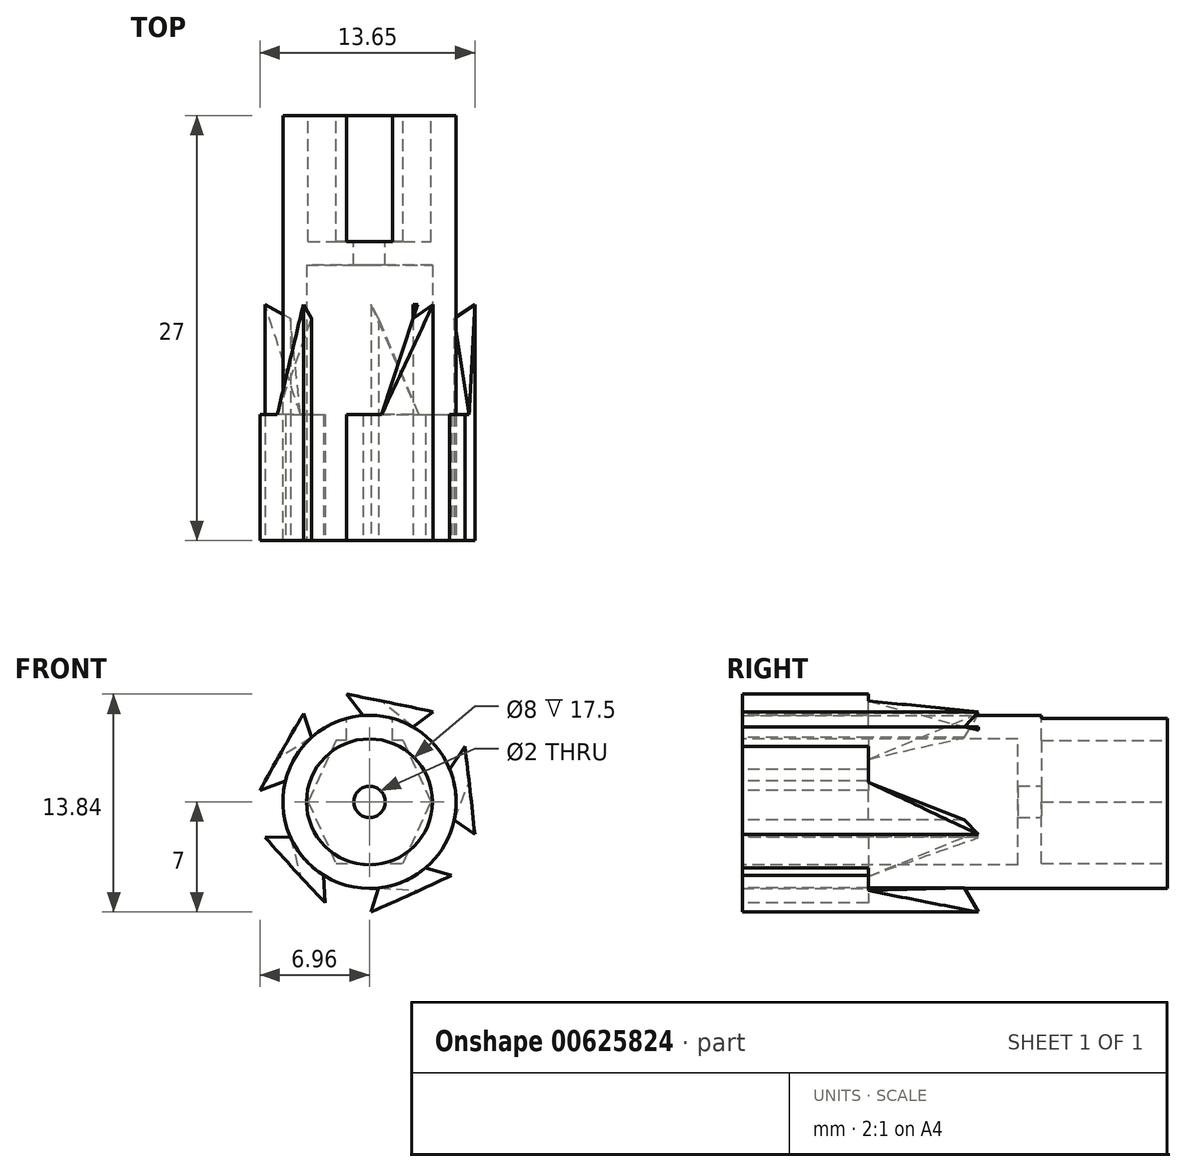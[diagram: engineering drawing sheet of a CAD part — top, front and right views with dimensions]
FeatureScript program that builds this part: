
annotation { "Feature Type Name" : "Feature", "Feature Type Description" : "" }
export const myFeature = defineFeature(function(context is Context, id is Id, definition is map)
    precondition{}
    {
        {
            var Q0;
            Q0=qCreatedBy(makeId("Front.planeOp"),FACE);
            var sketch = newSketch(context, id + "F0", { "sketchPlane" : qUnion([Q0])});
            skCircle(sketch, "E0", {"center": v(0, 0) * mm, "radius": 5.5 * mm});
            skSolve(sketch);
        }
        {
            var Q0;
            Q0=makeQuery(id+"F0.imprint","IMPRINT",FACE,{"disambiguationData":[TD([[makeQuery(id+"F0.imprint","IMPRINT",EDGE,{"derivedFrom":sQuery(id+"F0.wireOp",EDGE,"E0")}),1.0]])]});
            extrude(context, id + "F1", {"entities" : qUnion([Q0]), "endBound" : BoundingType.SYMMETRIC, "depth" : 27 * mm, "offsetDistance" : 25 * mm});
        }
        {
            var Q0;
            Q0=makeQuery(id+"F1.opExtrude","CAP_FACE",FACE,{"disambiguationData":[OSD([sQuery(id+"F0.wireOp",EDGE,"E0")])],"isStart":false});
            var sketch = newSketch(context, id + "F2", { "sketchPlane" : qUnion([Q0])});
            skCircle(sketch, "E1", {"center": v(0, 0) * mm, "radius": 4 * mm});
            skSolve(sketch);
        }
        {
            var Q0;
            Q0 = qSketchRegion(id + "F2", true);
            extrude(context, id + "F3", {"entities" : qUnion([Q0]), "operationType" : NewBodyOperationType.REMOVE, "oppositeDirection" : true, "depth" : 17.5 * mm, "offsetDistance" : 25 * mm});
        }
        {
            var Q0;
            Q0=makeQuery(id+"F1.opExtrude","CAP_FACE",FACE,{"disambiguationData":[OSD([sQuery(id+"F0.wireOp",EDGE,"E0")])],"isStart":true});
            var sketch = newSketch(context, id + "F4", { "sketchPlane" : qUnion([Q0])});
            skLineSegment(sketch, "E2", {"start": v(0, 3.9) * mm, "end": v(0, -3.9) * mm});
            skLineSegment(sketch, "E3", {"start": v(0, -3.9) * mm, "end": v(0, -5.5) * mm});
            skLineSegment(sketch, "E4", {"start": v(0, 3.9) * mm, "end": v(0, 5.5) * mm});
            skPoint(sketch, "E5.startSnap0", {"position": v(0, 0) * mm});
            skLineSegment(sketch, "E6", {"start": v(-3.9, 0) * mm, "end": v(3.9, 0) * mm});
            skLineSegment(sketch, "E7", {"start": v(-2.14, 3.9) * mm, "end": v(2.14, 3.9) * mm});
            skLineSegment(sketch, "E8", {"start": v(2.14, 3.9) * mm, "end": v(3.9, 0) * mm});
            skLineSegment(sketch, "E9", {"start": v(3.9, 0) * mm, "end": v(2.14, -3.9) * mm});
            skLineSegment(sketch, "E10", {"start": v(2.14, -3.9) * mm, "end": v(-2.14, -3.9) * mm});
            skLineSegment(sketch, "E11", {"start": v(-2.14, -3.9) * mm, "end": v(-3.9, 0) * mm});
            skLineSegment(sketch, "E12", {"start": v(-2.14, 3.9) * mm, "end": v(-3.9, 0) * mm});
            skSolve(sketch);
        }
        {
            var Q0;
            Q0 = qSketchRegion(id + "F4", true);
            extrude(context, id + "F5", {"entities" : qUnion([Q0]), "operationType" : NewBodyOperationType.REMOVE, "oppositeDirection" : true, "depth" : 8 * mm, "offsetDistance" : 25 * mm});
        }
        {
            var Q0;
            Q0=makeQuery(id+"F5.boolean.opBoolean","COPY",FACE,{"derivedFrom":makeQuery(id+"F5.opExtrude","CAP_FACE",FACE,{"disambiguationData":[OSD([sQuery(id+"F4.wireOp",EDGE,"E7"),sQuery(id+"F4.wireOp",EDGE,"E8"),sQuery(id+"F4.wireOp",EDGE,"E9"),sQuery(id+"F4.wireOp",EDGE,"E10"),sQuery(id+"F4.wireOp",EDGE,"E11"),sQuery(id+"F4.wireOp",EDGE,"E12")])],"isStart":false})});
            var sketch = newSketch(context, id + "F6", { "sketchPlane" : qUnion([Q0])});
            skCircle(sketch, "E13", {"center": v(0, 0) * mm, "radius": 1 * mm});
            skSolve(sketch);
        }
        {
            var Q0;
            Q0=makeQuery(id+"F6.imprint","IMPRINT",FACE,{"disambiguationData":[TD([[makeQuery(id+"F6.imprint","IMPRINT",EDGE,{"derivedFrom":sQuery(id+"F6.wireOp",EDGE,"E13")}),1.0]])]});
            extrude(context, id + "F7", {"entities" : qUnion([Q0]), "operationType" : NewBodyOperationType.REMOVE, "oppositeDirection" : true, "depth" : 1.5 * mm, "offsetDistance" : 25 * mm});
        }
        {
            var Q0;
            Q0=makeQuery(id+"F1.opExtrude","CAP_FACE",FACE,{"disambiguationData":[OSD([sQuery(id+"F0.wireOp",EDGE,"E0")])],"isStart":true});
            var sketch = newSketch(context, id + "F8", { "sketchPlane" : qUnion([Q0])});
            skLineSegment(sketch, "E14", {"start": v(-1.47, 3.9) * mm, "end": v(-1.47, 5.3) * mm});
            skLineSegment(sketch, "E15", {"start": v(1.47, 3.9) * mm, "end": v(1.47, 5.3) * mm});
            skSolve(sketch);
        }
        {
            var Q0;
            {var subQ0=sQuery(id+"F8.wireOp",EDGE,"E14");Q0=makeQuery(id+"F8.imprint","IMPRINT",FACE,{"disambiguationData":[TD([[makeQuery(id+"F8.imprint","IMPRINT",EDGE,{"derivedFrom":subQ0}),-1.0]])]});}
            extrude(context, id + "F9", {"entities" : qUnion([Q0]), "operationType" : NewBodyOperationType.REMOVE, "oppositeDirection" : true, "depth" : 8 * mm, "offsetDistance" : 25 * mm});
        }
        {
            var Q0;
            Q0=makeQuery(id+"F1.opExtrude","CAP_FACE",FACE,{"disambiguationData":[OSD([sQuery(id+"F0.wireOp",EDGE,"E0")])],"isStart":false});
            var sketch = newSketch(context, id + "F10", { "sketchPlane" : qUnion([Q0])});
            skLineSegment(sketch, "E16", {"start": v(-0.4, 5.49) * mm, "end": v(-1.47, 6.84) * mm});
            skLineSegment(sketch, "E17", {"start": v(2.75, 4.76) * mm, "end": v(4.03, 5.72) * mm});
            skArc(sketch, "E18", {"start": v(4.03, 5.72) * mm, "mid": v(1.28, 6.3) * mm, "end": v(-1.47, 6.84) * mm});
            skArc(sketch, "E19", {"start": v(2.75, 4.76) * mm, "mid": v(1.23, 5.36) * mm, "end": v(-0.4, 5.49) * mm});
            skSolve(sketch);
        }
        {
            var Q0;
            Q0 = qSketchRegion(id + "F10", true);
            extrude(context, id + "F11", {"entities" : qUnion([Q0]), "oppositeDirection" : true, "depth" : 15 * mm, "offsetDistance" : 25 * mm});
        }
        {
            var Q0;
            Q0=makeQuery(id+"F11.opExtrude","SWEPT_FACE",FACE,{"disambiguationData":[OSD([sQuery(id+"F10.wireOp",EDGE,"E16")])]});
            var sketch = newSketch(context, id + "F12", { "sketchPlane" : qUnion([Q0])});
            skLineSegment(sketch, "E20", {"start": v(-1.5, 4.55) * mm, "end": v(5.5, 4.55) * mm});
            skLineSegment(sketch, "E21", {"start": v(5.5, 4.55) * mm, "end": v(5.5, 6.28) * mm});
            skLineSegment(sketch, "E22", {"start": v(5.5, 6.28) * mm, "end": v(-1.5, 6.28) * mm});
            skLineSegment(sketch, "E23", {"start": v(-1.5, 6.28) * mm, "end": v(-1.5, 4.55) * mm});
            skSolve(sketch);
        }
        {
            var Q0;
            Q0 = qSketchRegion(id + "F12", true);
            extrude(context, id + "F13", {"entities" : qUnion([Q0]), "operationType" : NewBodyOperationType.REMOVE, "oppositeDirection" : true, "depth" : 25 * mm, "offsetDistance" : 25 * mm});
        }
        {
            var Q0;
            Q0=makeQuery(id+"F11.opExtrude","CAP_FACE",FACE,{"disambiguationData":[OSD([sQuery(id+"F10.wireOp",EDGE,"E16"),sQuery(id+"F10.wireOp",EDGE,"E17"),sQuery(id+"F10.wireOp",EDGE,"E18"),sQuery(id+"F10.wireOp",EDGE,"E19")])],"isStart":false});
            var sketch = newSketch(context, id + "F14", { "sketchPlane" : qUnion([Q0])});
            skLineSegment(sketch, "E24", {"start": v(-2.75, 4.76) * mm, "end": v(-0.77, 6.4) * mm});
            skLineSegment(sketch, "E25", {"start": v(-0.77, 6.4) * mm, "end": v(0.4, 5.49) * mm});
            skArc(sketch, "E26", {"start": v(0.4, 5.49) * mm, "mid": v(-1.23, 5.36) * mm, "end": v(-2.75, 4.76) * mm});
            skSolve(sketch);
        }
        {
            var Q0;
            Q0 = qSketchRegion(id + "F14", true);
            extrude(context, id + "F15", {"entities" : qUnion([Q0]), "operationType" : NewBodyOperationType.REMOVE, "oppositeDirection" : true, "depth" : 7 * mm, "offsetDistance" : 25 * mm});
        }
        {
            var Q0;
            Q0=makeQuery(id+"F15.boolean.opBoolean","COPY",FACE,{"derivedFrom":makeQuery(id+"F15.opExtrude","SWEPT_FACE",FACE,{"disambiguationData":[OSD([sQuery(id+"F14.wireOp",EDGE,"E24")])]})});
            var sketch = newSketch(context, id + "F16", { "sketchPlane" : qUnion([Q0])});
            skLineSegment(sketch, "E27", {"start": v(-3.5, 5.5) * mm, "end": v(-3.5, -1.5) * mm});
            skLineSegment(sketch, "E28", {"start": v(-3.5, 5.5) * mm, "end": v(-0.55, -1.5) * mm});
            skLineSegment(sketch, "E29", {"start": v(-0.55, -1.5) * mm, "end": v(-3.5, -1.5) * mm});
            skSolve(sketch);
        }
        {
            var Q0;
            Q0 = qSketchRegion(id + "F16", true);
            extrude(context, id + "F17", {"entities" : qUnion([Q0]), "operationType" : NewBodyOperationType.REMOVE, "oppositeDirection" : true, "depth" : 7 * mm, "offsetDistance" : 25 * mm});
        }
        {
            var Q0;
            Q0=makeQuery(id+"F11.opExtrude","SWEPT_BODY",BODY,{"disambiguationData":[OSD([sQuery(id+"F10.wireOp",EDGE,"E16"),sQuery(id+"F10.wireOp",EDGE,"E17"),sQuery(id+"F10.wireOp",EDGE,"E18"),sQuery(id+"F10.wireOp",EDGE,"E19")])]});
            var Q1;
            Q1=makeQuery(id+"FzrlKFucqWlIOBW_2.boolean.opBoolean","MERGE",FACE,{"derivedFrom":[makeQuery(id+"F1.opExtrude","SWEPT_FACE",FACE,{"disambiguationData":[OSD([sQuery(id+"F0.wireOp",EDGE,"E0")])]}),makeQuery(id+"FzrlKFucqWlIOBW_2.opExtrude","SWEPT_FACE",FACE,{"disambiguationData":[OSD([sQuery(id+"F10.wireOp",EDGE,"E19")])]})]});
            circularPattern(context, id + "F18", {"entities" : qUnion([Q0]), "axis" : qUnion([Q1]), "angle" : 360 * degree, "instanceCount" : 5, "equalSpace" : true});
        }
    });
